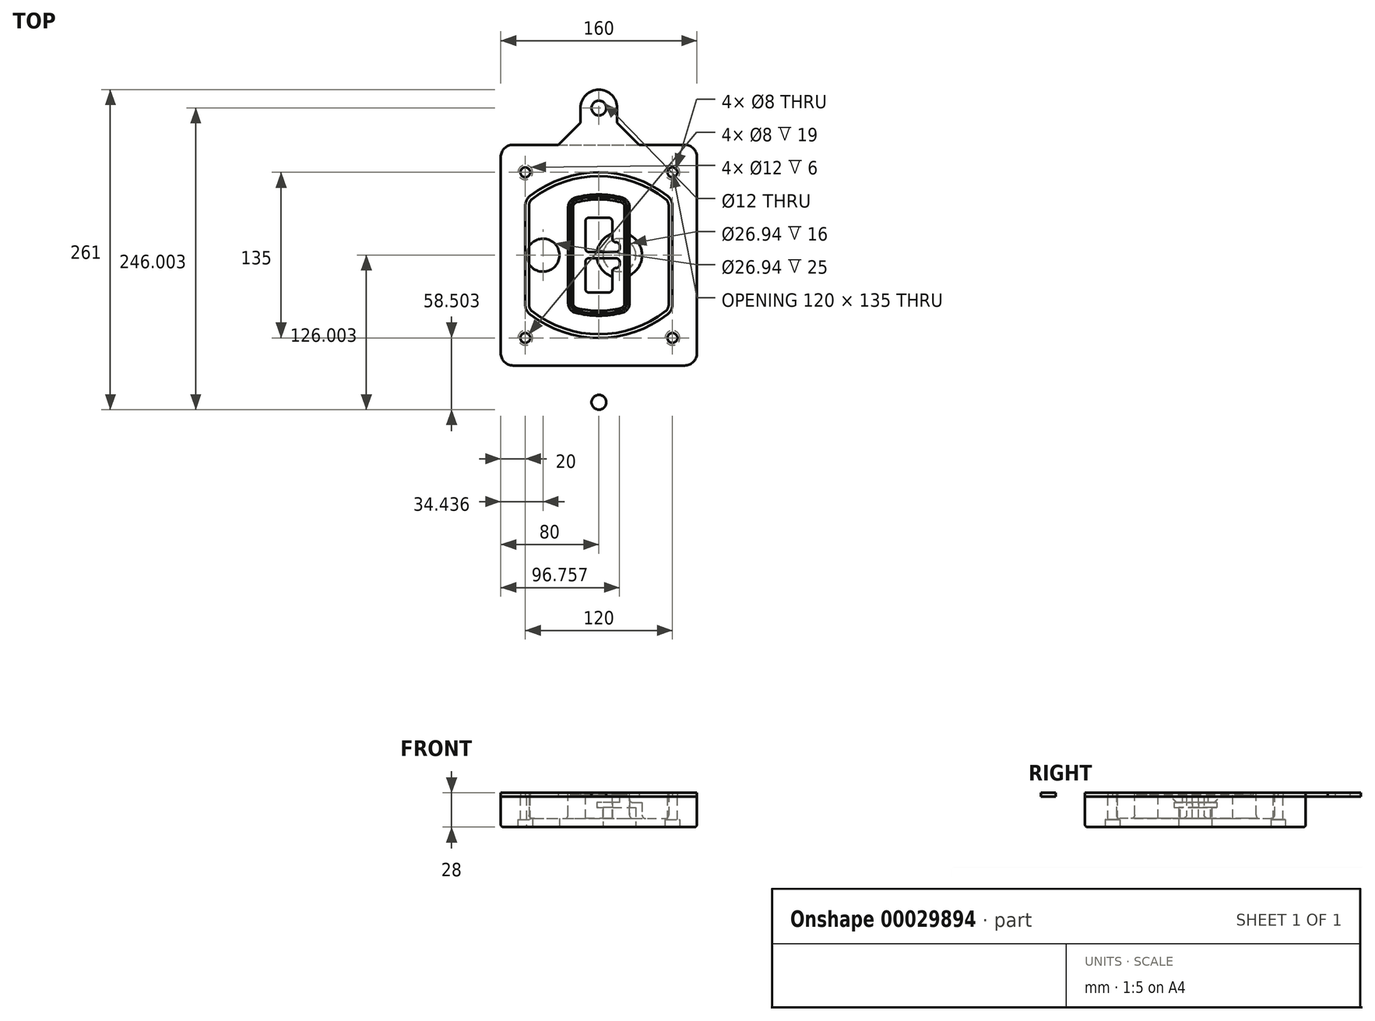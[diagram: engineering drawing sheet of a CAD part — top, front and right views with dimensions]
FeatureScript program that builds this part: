
annotation { "Feature Type Name" : "Feature", "Feature Type Description" : "" }
export const myFeature = defineFeature(function(context is Context, id is Id, definition is map)
    precondition{}
    {
        {
            var Q0;
            Q0=qCreatedBy(makeId("Top.planeOp"),FACE);
            var sketch = newSketch(context, id + "F0", { "sketchPlane" : qUnion([Q0])});
            skPoint(sketch, "E0.rect.middle", {"position": v(0, 0) * mm});
            skLineSegment(sketch, "E1.bottom", {"start": v(24.05, 28.38) * mm, "end": v(164.05, 28.38) * mm});
            skLineSegment(sketch, "E1.top", {"start": v(24.05, 208.38) * mm, "end": v(164.05, 208.38) * mm});
            skLineSegment(sketch, "E1.left", {"start": v(14.05, 38.38) * mm, "end": v(14.05, 198.38) * mm});
            skLineSegment(sketch, "E1.right", {"start": v(174.05, 38.38) * mm, "end": v(174.05, 198.38) * mm});
            skLineSegment(sketch, "E2", {"start": v(14.05, 208.38) * mm, "end": v(174.05, 28.38) * mm, "construction": true});
            skLineSegment(sketch, "E3", {"start": v(174.05, 208.38) * mm, "end": v(14.05, 28.38) * mm, "construction": true});
            skCircle(sketch, "E4", {"center": v(34.05, 185.88) * mm, "radius": 4 * mm});
            skCircle(sketch, "E5", {"center": v(154.05, 185.88) * mm, "radius": 4 * mm});
            skCircle(sketch, "E6", {"center": v(154.05, 50.88) * mm, "radius": 4 * mm});
            skCircle(sketch, "E7", {"center": v(34.05, 50.88) * mm, "radius": 4 * mm});
            skLineSegment(sketch, "E8", {"start": v(34.05, 185.88) * mm, "end": v(154.05, 185.88) * mm, "construction": true});
            skLineSegment(sketch, "E9", {"start": v(154.05, 185.88) * mm, "end": v(154.05, 50.88) * mm, "construction": true});
            skLineSegment(sketch, "E10", {"start": v(154.05, 50.88) * mm, "end": v(34.05, 50.88) * mm, "construction": true});
            skLineSegment(sketch, "E11", {"start": v(34.05, 50.88) * mm, "end": v(34.05, 185.88) * mm, "construction": true});
            skLineSegment(sketch, "E12", {"start": v(34.05, 158.68) * mm, "end": v(34.05, 78.09) * mm});
            skLineSegment(sketch, "E13", {"start": v(154.05, 158.68) * mm, "end": v(154.05, 78.09) * mm});
            skArc(sketch, "E14", {"start": v(150.2, 166.56) * mm, "mid": v(94.05, 185.88) * mm, "end": v(37.9, 166.56) * mm});
            skArc(sketch, "E15", {"start": v(37.9, 70.2) * mm, "mid": v(94.05, 50.88) * mm, "end": v(150.2, 70.2) * mm});
            skLineSegment(sketch, "E16", {"start": v(34.05, 118.38) * mm, "end": v(154.05, 118.38) * mm, "construction": true});
            skPoint(sketch, "E17.visualSharp", {"position": v(34.05, 73.38) * mm});
            skArc(sketch, "E17.filletArc", {"start": v(34.05, 78.09) * mm, "mid": v(35.06, 73.7) * mm, "end": v(37.9, 70.2) * mm});
            skPoint(sketch, "E18.visualSharp", {"position": v(34.05, 163.38) * mm});
            skArc(sketch, "E18.filletArc", {"start": v(37.9, 166.56) * mm, "mid": v(35.06, 163.06) * mm, "end": v(34.05, 158.68) * mm});
            skPoint(sketch, "E19.visualSharp", {"position": v(154.05, 163.38) * mm});
            skArc(sketch, "E19.filletArc", {"start": v(154.05, 158.68) * mm, "mid": v(153.04, 163.06) * mm, "end": v(150.2, 166.56) * mm});
            skPoint(sketch, "E20.visualSharp", {"position": v(154.05, 73.38) * mm});
            skArc(sketch, "E20.filletArc", {"start": v(150.2, 70.2) * mm, "mid": v(153.04, 73.7) * mm, "end": v(154.05, 78.09) * mm});
            skPoint(sketch, "E21.visualSharp", {"position": v(14.05, 208.38) * mm});
            skArc(sketch, "E21.filletArc", {"start": v(24.05, 208.38) * mm, "mid": v(16.98, 205.45) * mm, "end": v(14.05, 198.38) * mm});
            skPoint(sketch, "E22.visualSharp", {"position": v(174.05, 208.38) * mm});
            skArc(sketch, "E22.filletArc", {"start": v(174.05, 198.38) * mm, "mid": v(171.12, 205.45) * mm, "end": v(164.05, 208.38) * mm});
            skPoint(sketch, "E23.visualSharp", {"position": v(174.05, 28.38) * mm});
            skArc(sketch, "E23.filletArc", {"start": v(164.05, 28.38) * mm, "mid": v(171.12, 31.31) * mm, "end": v(174.05, 38.38) * mm});
            skPoint(sketch, "E24.visualSharp", {"position": v(14.05, 28.38) * mm});
            skArc(sketch, "E24.filletArc", {"start": v(14.05, 38.38) * mm, "mid": v(16.98, 31.31) * mm, "end": v(24.05, 28.38) * mm});
            skArc(sketch, "E25.0", {"start": v(151.05, 158.68) * mm, "mid": v(150.34, 161.75) * mm, "end": v(148.36, 164.2) * mm});
            skLineSegment(sketch, "E25.1", {"start": v(151.05, 158.68) * mm, "end": v(151.05, 78.09) * mm});
            skArc(sketch, "E25.2", {"start": v(148.36, 72.57) * mm, "mid": v(150.34, 75.02) * mm, "end": v(151.05, 78.09) * mm});
            skArc(sketch, "E25.3", {"start": v(39.74, 72.57) * mm, "mid": v(94.05, 53.88) * mm, "end": v(148.36, 72.57) * mm});
            skArc(sketch, "E25.4", {"start": v(37.05, 78.09) * mm, "mid": v(37.76, 75.02) * mm, "end": v(39.74, 72.57) * mm});
            skArc(sketch, "E25.5", {"start": v(148.36, 164.2) * mm, "mid": v(94.05, 182.88) * mm, "end": v(39.74, 164.2) * mm});
            skLineSegment(sketch, "E25.6", {"start": v(37.05, 158.68) * mm, "end": v(37.05, 78.09) * mm});
            skArc(sketch, "E25.7", {"start": v(39.74, 164.2) * mm, "mid": v(37.76, 161.75) * mm, "end": v(37.05, 158.68) * mm});
            skArc(sketch, "E26.0", {"start": v(35.43, 169.71) * mm, "mid": v(31.47, 164.82) * mm, "end": v(30.05, 158.68) * mm});
            skArc(sketch, "E26.1", {"start": v(152.67, 169.71) * mm, "mid": v(94.05, 189.88) * mm, "end": v(35.43, 169.71) * mm});
            skArc(sketch, "E26.2", {"start": v(158.05, 158.68) * mm, "mid": v(156.63, 164.82) * mm, "end": v(152.67, 169.71) * mm});
            skLineSegment(sketch, "E26.3", {"start": v(158.05, 158.68) * mm, "end": v(158.05, 78.09) * mm});
            skArc(sketch, "E26.4", {"start": v(152.67, 67.05) * mm, "mid": v(156.63, 71.95) * mm, "end": v(158.05, 78.09) * mm});
            skLineSegment(sketch, "E26.5", {"start": v(30.05, 158.68) * mm, "end": v(30.05, 78.09) * mm});
            skArc(sketch, "E26.6", {"start": v(35.43, 67.05) * mm, "mid": v(94.05, 46.88) * mm, "end": v(152.67, 67.05) * mm});
            skArc(sketch, "E26.7", {"start": v(30.05, 78.09) * mm, "mid": v(31.47, 71.95) * mm, "end": v(35.43, 67.05) * mm});
            skSolve(sketch);
        }
        {
            var Q0;
            Q0=makeQuery(id+"F0.imprint","IMPRINT",FACE,{"disambiguationData":[TD([[makeQuery(id+"F0.imprint","IMPRINT",EDGE,{"derivedFrom":sQuery(id+"F0.wireOp",EDGE,"E1.bottom")}),1.0]])]});
            var Q1;
            Q1=makeQuery(id+"F0.imprint","IMPRINT",FACE,{"disambiguationData":[TD([[makeQuery(id+"F0.imprint","IMPRINT",EDGE,{"derivedFrom":sQuery(id+"F0.wireOp",EDGE,"E12")}),1.0]])]});
            var Q2;
            Q2=makeQuery(id+"F0.imprint","IMPRINT",FACE,{"disambiguationData":[TD([[makeQuery(id+"F0.imprint","IMPRINT",EDGE,{"derivedFrom":sQuery(id+"F0.wireOp",EDGE,"E25.0")}),1.0]])]});
            var Q3;
            Q3=makeQuery(id+"F0.imprint","IMPRINT",FACE,{"disambiguationData":[TD([[makeQuery(id+"F0.imprint","IMPRINT",EDGE,{"derivedFrom":sQuery(id+"F0.wireOp",EDGE,"E12")}),-1.0]])]});
            extrude(context, id + "F1", {"entities" : qUnion([Q0, Q1, Q2, Q3]), "oppositeDirection" : true, "depth" : 25 * mm});
        }
        {
            var Q0;
            Q0=makeQuery(id+"F0.imprint","IMPRINT",FACE,{"disambiguationData":[TD([[makeQuery(id+"F0.imprint","IMPRINT",EDGE,{"derivedFrom":sQuery(id+"F0.wireOp",EDGE,"E12")}),1.0]])]});
            extrude(context, id + "F2", {"entities" : qUnion([Q0]), "operationType" : NewBodyOperationType.ADD, "depth" : 3 * mm});
        }
        {
            var Q0;
            Q0=makeQuery(id+"F0.imprint","IMPRINT",FACE,{"disambiguationData":[TD([[makeQuery(id+"F0.imprint","IMPRINT",EDGE,{"derivedFrom":sQuery(id+"F0.wireOp",EDGE,"E25.0")}),1.0]])]});
            extrude(context, id + "F3", {"entities" : qUnion([Q0]), "operationType" : NewBodyOperationType.REMOVE, "oppositeDirection" : true, "depth" : 18 * mm});
        }
        {
            var Q0;
            Q0=makeQuery(id+"F2.opExtrude","CAP_FACE",FACE,{"disambiguationData":[OSD([sQuery(id+"F0.wireOp",EDGE,"E12"),sQuery(id+"F0.wireOp",EDGE,"E13"),sQuery(id+"F0.wireOp",EDGE,"E14"),sQuery(id+"F0.wireOp",EDGE,"E15"),sQuery(id+"F0.wireOp",EDGE,"E17.filletArc"),sQuery(id+"F0.wireOp",EDGE,"E18.filletArc"),sQuery(id+"F0.wireOp",EDGE,"E19.filletArc"),sQuery(id+"F0.wireOp",EDGE,"E20.filletArc"),sQuery(id+"F0.wireOp",EDGE,"E25.0"),sQuery(id+"F0.wireOp",EDGE,"E25.1"),sQuery(id+"F0.wireOp",EDGE,"E25.2"),sQuery(id+"F0.wireOp",EDGE,"E25.3"),sQuery(id+"F0.wireOp",EDGE,"E25.4"),sQuery(id+"F0.wireOp",EDGE,"E25.5"),sQuery(id+"F0.wireOp",EDGE,"E25.6"),sQuery(id+"F0.wireOp",EDGE,"E25.7")])],"isStart":false});
            var sketch = newSketch(context, id + "F4", { "sketchPlane" : qUnion([Q0])});
            skArc(sketch, "E27.0", {"start": v(74.97, 71.41) * mm, "mid": v(94.05, 68.88) * mm, "end": v(113.13, 71.41) * mm});
            skArc(sketch, "E28.0", {"start": v(113.13, 165.35) * mm, "mid": v(94.05, 167.88) * mm, "end": v(74.97, 165.35) * mm});
            skLineSegment(sketch, "E29", {"start": v(69.05, 157.63) * mm, "end": v(69.05, 79.14) * mm});
            skLineSegment(sketch, "E30", {"start": v(119.05, 157.63) * mm, "end": v(119.05, 79.14) * mm});
            skLineSegment(sketch, "E31", {"start": v(69.05, 163.48) * mm, "end": v(119.05, 163.48) * mm, "construction": true});
            skLineSegment(sketch, "E32", {"start": v(69.05, 73.28) * mm, "end": v(119.05, 73.28) * mm, "construction": true});
            skPoint(sketch, "E33.visualSharp", {"position": v(69.05, 163.48) * mm});
            skArc(sketch, "E33.filletArc", {"start": v(74.97, 165.35) * mm, "mid": v(70.7, 162.5) * mm, "end": v(69.05, 157.63) * mm});
            skPoint(sketch, "E34.visualSharp", {"position": v(119.05, 163.48) * mm});
            skArc(sketch, "E34.filletArc", {"start": v(119.05, 157.63) * mm, "mid": v(117.4, 162.5) * mm, "end": v(113.13, 165.35) * mm});
            skPoint(sketch, "E35.visualSharp", {"position": v(119.05, 73.28) * mm});
            skArc(sketch, "E35.filletArc", {"start": v(113.13, 71.41) * mm, "mid": v(117.4, 74.27) * mm, "end": v(119.05, 79.14) * mm});
            skPoint(sketch, "E36.visualSharp", {"position": v(69.05, 73.28) * mm});
            skArc(sketch, "E36.filletArc", {"start": v(69.05, 79.14) * mm, "mid": v(70.7, 74.27) * mm, "end": v(74.97, 71.41) * mm});
            skArc(sketch, "E37.0", {"start": v(148.36, 164.2) * mm, "mid": v(94.05, 182.88) * mm, "end": v(39.74, 164.2) * mm});
            skArc(sketch, "E37.1", {"start": v(39.74, 164.2) * mm, "mid": v(37.76, 161.75) * mm, "end": v(37.05, 158.68) * mm});
            skLineSegment(sketch, "E37.2", {"start": v(37.05, 158.68) * mm, "end": v(37.05, 78.09) * mm});
            skArc(sketch, "E37.3", {"start": v(37.05, 78.09) * mm, "mid": v(37.76, 75.02) * mm, "end": v(39.74, 72.57) * mm});
            skArc(sketch, "E37.4", {"start": v(39.74, 72.57) * mm, "mid": v(94.05, 53.88) * mm, "end": v(148.36, 72.57) * mm});
            skArc(sketch, "E37.5", {"start": v(148.36, 72.57) * mm, "mid": v(150.34, 75.02) * mm, "end": v(151.05, 78.09) * mm});
            skLineSegment(sketch, "E37.6", {"start": v(151.05, 158.68) * mm, "end": v(151.05, 78.09) * mm});
            skArc(sketch, "E37.7", {"start": v(151.05, 158.68) * mm, "mid": v(150.34, 161.75) * mm, "end": v(148.36, 164.2) * mm});
            skLineSegment(sketch, "E38.0", {"start": v(117.05, 157.63) * mm, "end": v(117.05, 79.14) * mm});
            skArc(sketch, "E38.1", {"start": v(112.61, 73.34) * mm, "mid": v(115.81, 75.49) * mm, "end": v(117.05, 79.14) * mm});
            skArc(sketch, "E38.2", {"start": v(75.49, 73.34) * mm, "mid": v(94.05, 70.88) * mm, "end": v(112.61, 73.34) * mm});
            skArc(sketch, "E38.3", {"start": v(71.05, 79.14) * mm, "mid": v(72.29, 75.49) * mm, "end": v(75.49, 73.34) * mm});
            skLineSegment(sketch, "E38.4", {"start": v(71.05, 157.63) * mm, "end": v(71.05, 79.14) * mm});
            skArc(sketch, "E38.5", {"start": v(117.05, 157.63) * mm, "mid": v(115.81, 161.28) * mm, "end": v(112.61, 163.42) * mm});
            skArc(sketch, "E38.6", {"start": v(75.49, 163.42) * mm, "mid": v(72.29, 161.28) * mm, "end": v(71.05, 157.63) * mm});
            skArc(sketch, "E38.7", {"start": v(112.61, 163.42) * mm, "mid": v(94.05, 165.88) * mm, "end": v(75.49, 163.42) * mm});
            skArc(sketch, "E39.0", {"start": v(115.05, 157.63) * mm, "mid": v(114.23, 160.06) * mm, "end": v(112.1, 161.5) * mm});
            skLineSegment(sketch, "E39.1", {"start": v(115.05, 157.63) * mm, "end": v(115.05, 79.14) * mm});
            skArc(sketch, "E39.2", {"start": v(112.1, 75.27) * mm, "mid": v(114.23, 76.7) * mm, "end": v(115.05, 79.14) * mm});
            skArc(sketch, "E39.3", {"start": v(76, 75.27) * mm, "mid": v(94.05, 72.88) * mm, "end": v(112.1, 75.27) * mm});
            skArc(sketch, "E39.4", {"start": v(73.05, 79.14) * mm, "mid": v(73.87, 76.7) * mm, "end": v(76, 75.27) * mm});
            skArc(sketch, "E39.5", {"start": v(112.1, 161.5) * mm, "mid": v(94.05, 163.88) * mm, "end": v(76, 161.5) * mm});
            skLineSegment(sketch, "E39.6", {"start": v(73.05, 157.63) * mm, "end": v(73.05, 79.14) * mm});
            skArc(sketch, "E39.7", {"start": v(76, 161.5) * mm, "mid": v(73.87, 160.06) * mm, "end": v(73.05, 157.63) * mm});
            skLineSegment(sketch, "E40", {"start": v(69.05, 118.38) * mm, "end": v(119.05, 118.38) * mm, "construction": true});
            skLineSegment(sketch, "E41", {"start": v(83.05, 123.88) * mm, "end": v(83.05, 145.88) * mm});
            skLineSegment(sketch, "E42", {"start": v(86.05, 148.88) * mm, "end": v(102.05, 148.88) * mm});
            skLineSegment(sketch, "E43", {"start": v(105.05, 145.88) * mm, "end": v(105.05, 131.88) * mm});
            skLineSegment(sketch, "E44", {"start": v(108.05, 128.88) * mm, "end": v(108.05, 128.88) * mm});
            skLineSegment(sketch, "E45", {"start": v(111.05, 125.88) * mm, "end": v(111.05, 123.88) * mm});
            skLineSegment(sketch, "E46", {"start": v(108.05, 120.88) * mm, "end": v(86.05, 120.88) * mm});
            skPoint(sketch, "E47.visualSharp", {"position": v(83.05, 148.88) * mm});
            skArc(sketch, "E47.filletArc", {"start": v(86.05, 148.88) * mm, "mid": v(83.93, 148) * mm, "end": v(83.05, 145.88) * mm});
            skPoint(sketch, "E48.visualSharp", {"position": v(105.05, 148.88) * mm});
            skArc(sketch, "E48.filletArc", {"start": v(105.05, 145.88) * mm, "mid": v(104.17, 148) * mm, "end": v(102.05, 148.88) * mm});
            skPoint(sketch, "E49.visualSharp", {"position": v(105.05, 128.88) * mm});
            skArc(sketch, "E49.filletArc", {"start": v(105.05, 131.88) * mm, "mid": v(105.93, 129.76) * mm, "end": v(108.05, 128.88) * mm});
            skPoint(sketch, "E50.visualSharp", {"position": v(111.05, 128.88) * mm});
            skArc(sketch, "E50.filletArc", {"start": v(111.05, 125.88) * mm, "mid": v(110.17, 128) * mm, "end": v(108.05, 128.88) * mm});
            skPoint(sketch, "E51.visualSharp", {"position": v(111.05, 120.88) * mm});
            skArc(sketch, "E51.filletArc", {"start": v(108.05, 120.88) * mm, "mid": v(110.17, 121.76) * mm, "end": v(111.05, 123.88) * mm});
            skPoint(sketch, "E52.visualSharp", {"position": v(83.05, 120.88) * mm});
            skArc(sketch, "E52.filletArc", {"start": v(83.05, 123.88) * mm, "mid": v(83.93, 121.76) * mm, "end": v(86.05, 120.88) * mm});
            skLineSegment(sketch, "E53.0.MirrorCS", {"start": v(108.05, 115.88) * mm, "end": v(86.05, 115.88) * mm});
            skArc(sketch, "E54.0.MirrorCS", {"start": v(83.05, 112.88) * mm, "mid": v(83.93, 115) * mm, "end": v(86.05, 115.88) * mm});
            skLineSegment(sketch, "E55.0.MirrorCS", {"start": v(83.05, 112.88) * mm, "end": v(83.05, 90.88) * mm});
            skArc(sketch, "E56.0.MirrorCS", {"start": v(86.05, 87.88) * mm, "mid": v(83.93, 88.76) * mm, "end": v(83.05, 90.88) * mm});
            skLineSegment(sketch, "E57.0.MirrorCS", {"start": v(86.05, 87.88) * mm, "end": v(102.05, 87.88) * mm});
            skArc(sketch, "E58.0.MirrorCS", {"start": v(105.05, 90.88) * mm, "mid": v(104.17, 88.76) * mm, "end": v(102.05, 87.88) * mm});
            skLineSegment(sketch, "E59.0.MirrorCS", {"start": v(105.05, 90.88) * mm, "end": v(105.05, 104.88) * mm});
            skArc(sketch, "E60.0.MirrorCS", {"start": v(105.05, 104.88) * mm, "mid": v(105.93, 107) * mm, "end": v(108.05, 107.88) * mm});
            skArc(sketch, "E61.0.MirrorCS", {"start": v(111.05, 110.88) * mm, "mid": v(110.17, 108.76) * mm, "end": v(108.05, 107.88) * mm});
            skLineSegment(sketch, "E62.0.MirrorCS", {"start": v(111.05, 110.88) * mm, "end": v(111.05, 112.88) * mm});
            skArc(sketch, "E63.0.MirrorCS", {"start": v(108.05, 115.88) * mm, "mid": v(110.17, 115) * mm, "end": v(111.05, 112.88) * mm});
            skSolve(sketch);
        }
        {
            var Q0;
            Q0=makeQuery(id+"F4.imprint","IMPRINT",FACE,{"disambiguationData":[TD([[makeQuery(id+"F4.imprint","IMPRINT",EDGE,{"derivedFrom":sQuery(id+"F4.wireOp",EDGE,"E27.0")}),1.0]])]});
            var Q1;
            Q1=makeQuery(id+"F4.imprint","IMPRINT",FACE,{"disambiguationData":[TD([[makeQuery(id+"F4.imprint","IMPRINT",EDGE,{"derivedFrom":sQuery(id+"F4.wireOp",EDGE,"E38.0")}),-1.0]])]});
            var Q2;
            Q2=makeQuery(id+"F4.imprint","IMPRINT",FACE,{"disambiguationData":[TD([[makeQuery(id+"F4.imprint","IMPRINT",EDGE,{"derivedFrom":sQuery(id+"F4.wireOp",EDGE,"E39.0")}),1.0]])]});
            extrude(context, id + "F5", {"entities" : qUnion([Q0, Q1, Q2]), "operationType" : NewBodyOperationType.ADD, "endBound" : BoundingType.UP_TO_NEXT, "oppositeDirection" : true, "depth" : 25 * mm});
        }
        {
            var Q0;
            Q0=makeQuery(id+"F4.imprint","IMPRINT",FACE,{"disambiguationData":[TD([[makeQuery(id+"F4.imprint","IMPRINT",EDGE,{"derivedFrom":sQuery(id+"F4.wireOp",EDGE,"E38.0")}),-1.0]])]});
            extrude(context, id + "F6", {"entities" : qUnion([Q0]), "operationType" : NewBodyOperationType.REMOVE, "oppositeDirection" : true, "depth" : 2 * mm});
        }
        {
            var Q0;
            Q0=makeQuery(id+"F1.opExtrude","CAP_FACE",FACE,{"disambiguationData":[OSD([sQuery(id+"F0.wireOp",EDGE,"E1.bottom"),sQuery(id+"F0.wireOp",EDGE,"E1.top"),sQuery(id+"F0.wireOp",EDGE,"E1.left"),sQuery(id+"F0.wireOp",EDGE,"E1.right"),sQuery(id+"F0.wireOp",EDGE,"E4"),sQuery(id+"F0.wireOp",EDGE,"E5"),sQuery(id+"F0.wireOp",EDGE,"E6"),sQuery(id+"F0.wireOp",EDGE,"E7"),sQuery(id+"F0.wireOp",EDGE,"E21.filletArc"),sQuery(id+"F0.wireOp",EDGE,"E22.filletArc"),sQuery(id+"F0.wireOp",EDGE,"E23.filletArc"),sQuery(id+"F0.wireOp",EDGE,"E24.filletArc")])],"isStart":false});
            var sketch = newSketch(context, id + "F7", { "sketchPlane" : qUnion([Q0])});
            skCircle(sketch, "E64", {"center": v(110.8, -118.38) * mm, "radius": 13.47 * mm});
            skCircle(sketch, "E65", {"center": v(48.49, -118.38) * mm, "radius": 13.47 * mm});
            skLineSegment(sketch, "E66", {"start": v(174.05, -118.38) * mm, "end": v(14.05, -118.38) * mm});
            skCircle(sketch, "E67", {"center": v(110.8, -118.38) * mm, "radius": 18.47 * mm});
            skCircle(sketch, "E68", {"center": v(154.05, -185.88) * mm, "radius": 6 * mm});
            skCircle(sketch, "E69", {"center": v(34.05, -185.88) * mm, "radius": 6 * mm});
            skCircle(sketch, "E70", {"center": v(34.05, -50.88) * mm, "radius": 6 * mm});
            skCircle(sketch, "E71", {"center": v(154.05, -50.88) * mm, "radius": 6 * mm});
            skSolve(sketch);
        }
        {
            var Q0;
            {var subQ1=sQuery(id+"F7.wireOp",EDGE,"E66");var subQ4=sQuery(id+"F7.wireOp",EDGE,"E64");var subQ6=makeQuery(id+"F7.imprint","INTERSECT",VERTEX,{"disambiguationData":[OD(0.0)],"derivedFrom":[subQ4,subQ1]});Q0=makeQuery(id+"F7.imprint","IMPRINT",FACE,{"disambiguationData":[TD([[makeQuery(id+"F7.imprint","IMPRINT",EDGE,{"disambiguationData":[TD([[subQ6,-1.0]])],"derivedFrom":subQ4}),-1.0]])]});}
            var Q1;
            {var subQ0=sQuery(id+"F7.wireOp",EDGE,"E66");var subQ1=sQuery(id+"F7.wireOp",EDGE,"E64");var subQ3=makeQuery(id+"F7.imprint","INTERSECT",VERTEX,{"disambiguationData":[OD(0.0)],"derivedFrom":[subQ1,subQ0]});Q1=makeQuery(id+"F7.imprint","IMPRINT",FACE,{"disambiguationData":[TD([[makeQuery(id+"F7.imprint","IMPRINT",EDGE,{"disambiguationData":[TD([[subQ3,-1.0]])],"derivedFrom":subQ1}),1.0]])]});}
            var Q2;
            {var subQ0=sQuery(id+"F7.wireOp",EDGE,"E66");var subQ1=sQuery(id+"F7.wireOp",EDGE,"E64");var subQ3=makeQuery(id+"F7.imprint","INTERSECT",VERTEX,{"disambiguationData":[OD(0.0)],"derivedFrom":[subQ1,subQ0]});Q2=makeQuery(id+"F7.imprint","IMPRINT",FACE,{"disambiguationData":[TD([[makeQuery(id+"F7.imprint","IMPRINT",EDGE,{"disambiguationData":[TD([[subQ3,1.0]])],"derivedFrom":subQ1}),1.0]])]});}
            var Q3;
            {var subQ1=sQuery(id+"F7.wireOp",EDGE,"E66");var subQ4=sQuery(id+"F7.wireOp",EDGE,"E64");var subQ6=makeQuery(id+"F7.imprint","INTERSECT",VERTEX,{"disambiguationData":[OD(0.0)],"derivedFrom":[subQ4,subQ1]});Q3=makeQuery(id+"F7.imprint","IMPRINT",FACE,{"disambiguationData":[TD([[makeQuery(id+"F7.imprint","IMPRINT",EDGE,{"disambiguationData":[TD([[subQ6,1.0]])],"derivedFrom":subQ4}),-1.0]])]});}
            extrude(context, id + "F8", {"entities" : qUnion([Q0, Q1, Q2, Q3]), "operationType" : NewBodyOperationType.ADD, "oppositeDirection" : true, "depth" : 20 * mm});
        }
        {
            var Q0;
            {var subQ0=sQuery(id+"F7.wireOp",EDGE,"E66");var subQ1=sQuery(id+"F7.wireOp",EDGE,"E64");var subQ3=makeQuery(id+"F7.imprint","INTERSECT",VERTEX,{"disambiguationData":[OD(0.0)],"derivedFrom":[subQ1,subQ0]});Q0=makeQuery(id+"F7.imprint","IMPRINT",FACE,{"disambiguationData":[TD([[makeQuery(id+"F7.imprint","IMPRINT",EDGE,{"disambiguationData":[TD([[subQ3,-1.0]])],"derivedFrom":subQ1}),1.0]])]});}
            var Q1;
            {var subQ0=sQuery(id+"F7.wireOp",EDGE,"E66");var subQ1=sQuery(id+"F7.wireOp",EDGE,"E64");var subQ3=makeQuery(id+"F7.imprint","INTERSECT",VERTEX,{"disambiguationData":[OD(0.0)],"derivedFrom":[subQ1,subQ0]});Q1=makeQuery(id+"F7.imprint","IMPRINT",FACE,{"disambiguationData":[TD([[makeQuery(id+"F7.imprint","IMPRINT",EDGE,{"disambiguationData":[TD([[subQ3,1.0]])],"derivedFrom":subQ1}),1.0]])]});}
            extrude(context, id + "F9", {"entities" : qUnion([Q0, Q1]), "operationType" : NewBodyOperationType.REMOVE, "oppositeDirection" : true, "depth" : 16 * mm});
        }
        {
            var Q0;
            {var subQ0=sQuery(id+"F7.wireOp",EDGE,"E66");var subQ1=sQuery(id+"F7.wireOp",EDGE,"E65");var subQ3=makeQuery(id+"F7.imprint","INTERSECT",VERTEX,{"disambiguationData":[OD(0.0)],"derivedFrom":[subQ1,subQ0]});Q0=makeQuery(id+"F7.imprint","IMPRINT",FACE,{"disambiguationData":[TD([[makeQuery(id+"F7.imprint","IMPRINT",EDGE,{"disambiguationData":[TD([[subQ3,-1.0]])],"derivedFrom":subQ1}),1.0]])]});}
            var Q1;
            {var subQ0=sQuery(id+"F7.wireOp",EDGE,"E66");var subQ1=sQuery(id+"F7.wireOp",EDGE,"E65");var subQ3=makeQuery(id+"F7.imprint","INTERSECT",VERTEX,{"disambiguationData":[OD(0.0)],"derivedFrom":[subQ1,subQ0]});Q1=makeQuery(id+"F7.imprint","IMPRINT",FACE,{"disambiguationData":[TD([[makeQuery(id+"F7.imprint","IMPRINT",EDGE,{"disambiguationData":[TD([[subQ3,1.0]])],"derivedFrom":subQ1}),1.0]])]});}
            extrude(context, id + "F10", {"entities" : qUnion([Q0, Q1]), "operationType" : NewBodyOperationType.REMOVE, "oppositeDirection" : true, "depth" : 25 * mm});
        }
        {
            var Q0;
            Q0=makeQuery(id+"F7.imprint","IMPRINT",FACE,{"disambiguationData":[TD([[makeQuery(id+"F7.imprint","IMPRINT",EDGE,{"derivedFrom":sQuery(id+"F7.wireOp",EDGE,"E68")}),1.0]])]});
            var Q1;
            Q1=makeQuery(id+"F7.imprint","IMPRINT",FACE,{"disambiguationData":[TD([[makeQuery(id+"F7.imprint","IMPRINT",EDGE,{"derivedFrom":makeQuery(id+"F1.opExtrude","CAP_EDGE",EDGE,{"disambiguationData":[OSD([sQuery(id+"F0.wireOp",EDGE,"E5")])],"isStart":false})}),-1.0]])]});
            var Q2;
            Q2=makeQuery(id+"F7.imprint","IMPRINT",FACE,{"disambiguationData":[TD([[makeQuery(id+"F7.imprint","IMPRINT",EDGE,{"derivedFrom":sQuery(id+"F7.wireOp",EDGE,"E69")}),1.0]])]});
            var Q3;
            Q3=makeQuery(id+"F7.imprint","IMPRINT",FACE,{"disambiguationData":[TD([[makeQuery(id+"F7.imprint","IMPRINT",EDGE,{"derivedFrom":makeQuery(id+"F1.opExtrude","CAP_EDGE",EDGE,{"disambiguationData":[OSD([sQuery(id+"F0.wireOp",EDGE,"E4")])],"isStart":false})}),-1.0]])]});
            var Q4;
            Q4=makeQuery(id+"F7.imprint","IMPRINT",FACE,{"disambiguationData":[TD([[makeQuery(id+"F7.imprint","IMPRINT",EDGE,{"derivedFrom":sQuery(id+"F7.wireOp",EDGE,"E70")}),1.0]])]});
            var Q5;
            Q5=makeQuery(id+"F7.imprint","IMPRINT",FACE,{"disambiguationData":[TD([[makeQuery(id+"F7.imprint","IMPRINT",EDGE,{"derivedFrom":makeQuery(id+"F1.opExtrude","CAP_EDGE",EDGE,{"disambiguationData":[OSD([sQuery(id+"F0.wireOp",EDGE,"E7")])],"isStart":false})}),-1.0]])]});
            var Q6;
            Q6=makeQuery(id+"F7.imprint","IMPRINT",FACE,{"disambiguationData":[TD([[makeQuery(id+"F7.imprint","IMPRINT",EDGE,{"derivedFrom":sQuery(id+"F7.wireOp",EDGE,"E71")}),1.0]])]});
            var Q7;
            Q7=makeQuery(id+"F7.imprint","IMPRINT",FACE,{"disambiguationData":[TD([[makeQuery(id+"F7.imprint","IMPRINT",EDGE,{"derivedFrom":makeQuery(id+"F1.opExtrude","CAP_EDGE",EDGE,{"disambiguationData":[OSD([sQuery(id+"F0.wireOp",EDGE,"E6")])],"isStart":false})}),-1.0]])]});
            extrude(context, id + "F11", {"entities" : qUnion([Q0, Q1, Q2, Q3, Q4, Q5, Q6, Q7]), "operationType" : NewBodyOperationType.REMOVE, "oppositeDirection" : true, "depth" : 6 * mm});
        }
        {
            var Q0;
            Q0=makeQuery(id+"F9.boolean.opBoolean","COPY",FACE,{"derivedFrom":makeQuery(id+"F9.opExtrude","CAP_FACE",FACE,{"disambiguationData":[OSD([sQuery(id+"F7.wireOp",EDGE,"E64")])],"isStart":false})});
            var sketch = newSketch(context, id + "F12", { "sketchPlane" : qUnion([Q0])});
            skArc(sketch, "E72.0", {"start": v(105.05, -100.83) * mm, "mid": v(96.62, -106.56) * mm, "end": v(92.5, -115.88) * mm});
            skArc(sketch, "E72.1", {"start": v(92.5, -120.88) * mm, "mid": v(96.62, -130.2) * mm, "end": v(105.05, -135.93) * mm});
            skLineSegment(sketch, "E73", {"start": v(92.5, -120.88) * mm, "end": v(108.05, -120.88) * mm});
            skLineSegment(sketch, "E74.0", {"start": v(108.05, -115.88) * mm, "end": v(92.5, -115.88) * mm});
            skArc(sketch, "E74.1", {"start": v(108.05, -115.88) * mm, "mid": v(110.17, -115) * mm, "end": v(111.05, -112.88) * mm});
            skLineSegment(sketch, "E74.2", {"start": v(111.05, -110.88) * mm, "end": v(111.05, -112.88) * mm});
            skArc(sketch, "E74.3", {"start": v(111.05, -110.88) * mm, "mid": v(110.17, -108.76) * mm, "end": v(108.05, -107.88) * mm});
            skArc(sketch, "E74.4", {"start": v(105.05, -104.88) * mm, "mid": v(105.93, -107) * mm, "end": v(108.05, -107.88) * mm});
            skLineSegment(sketch, "E74.5", {"start": v(105.05, -100.83) * mm, "end": v(105.05, -104.88) * mm});
            skLineSegment(sketch, "E74.7", {"start": v(108.05, -120.88) * mm, "end": v(92.5, -120.88) * mm});
            skArc(sketch, "E74.8", {"start": v(108.05, -120.88) * mm, "mid": v(110.17, -121.76) * mm, "end": v(111.05, -123.88) * mm});
            skLineSegment(sketch, "E74.9", {"start": v(111.05, -125.88) * mm, "end": v(111.05, -123.88) * mm});
            skArc(sketch, "E74.10", {"start": v(111.05, -125.88) * mm, "mid": v(110.17, -128) * mm, "end": v(108.05, -128.88) * mm});
            skArc(sketch, "E74.11", {"start": v(105.05, -131.88) * mm, "mid": v(105.93, -129.76) * mm, "end": v(108.05, -128.88) * mm});
            skLineSegment(sketch, "E74.12", {"start": v(105.05, -135.93) * mm, "end": v(105.05, -131.88) * mm});
            skPoint(sketch, "E75.orphan", {"position": v(105.05, -145.88) * mm});
            skPoint(sketch, "E76.orphan", {"position": v(86.05, -120.88) * mm});
            skPoint(sketch, "E77.orphan", {"position": v(86.05, -115.88) * mm});
            skPoint(sketch, "E78.orphan", {"position": v(105.05, -90.88) * mm});
            skSolve(sketch);
        }
        {
            var Q0;
            {var subQ7=sQuery(id+"F12.wireOp",EDGE,"E72.0");var subQ14=sQuery(id+"F12.wireOp",EDGE,"E72.1");var subQ16=sQuery(id+"F12.wireOp",EDGE,"E74.1");var subQ18=sQuery(id+"F12.wireOp",EDGE,"E74.8");Q0=qUnion([makeQuery(id+"F12.imprint","IMPRINT",FACE,{"disambiguationData":[TD([[makeQuery(id+"F12.imprint","IMPRINT",EDGE,{"derivedFrom":subQ7}),1.0]])]}),makeQuery(id+"F12.imprint","IMPRINT",FACE,{"disambiguationData":[TD([[makeQuery(id+"F12.imprint","IMPRINT",EDGE,{"derivedFrom":subQ14}),1.0]])]}),makeQuery(id+"F12.imprint","IMPRINT",FACE,{"disambiguationData":[TD([[makeQuery(id+"F12.imprint","IMPRINT",EDGE,{"derivedFrom":subQ16}),1.0]])]}),makeQuery(id+"F12.imprint","IMPRINT",FACE,{"disambiguationData":[TD([[makeQuery(id+"F12.imprint","IMPRINT",EDGE,{"derivedFrom":subQ18}),-1.0]])]})]);}
            var Q1;
            Q1=makeQuery(id+"F5.boolean.opBoolean","SPLIT",FACE,{"disambiguationData":[TD([makeQuery(id+"F5.opExtrude","SWEPT_FACE",FACE,{"disambiguationData":[OSD([sQuery(id+"F4.wireOp",EDGE,"E41")])]})])],"derivedFrom":makeQuery(id+"F3.boolean.opBoolean","COPY",FACE,{"derivedFrom":makeQuery(id+"F3.opExtrude","CAP_FACE",FACE,{"disambiguationData":[OSD([sQuery(id+"F0.wireOp",EDGE,"E25.0"),sQuery(id+"F0.wireOp",EDGE,"E25.1"),sQuery(id+"F0.wireOp",EDGE,"E25.2"),sQuery(id+"F0.wireOp",EDGE,"E25.3"),sQuery(id+"F0.wireOp",EDGE,"E25.4"),sQuery(id+"F0.wireOp",EDGE,"E25.5"),sQuery(id+"F0.wireOp",EDGE,"E25.6"),sQuery(id+"F0.wireOp",EDGE,"E25.7")])],"isStart":false})})});
            extrude(context, id + "F13", {"entities" : qUnion([Q0]), "operationType" : NewBodyOperationType.REMOVE, "endBound" : BoundingType.UP_TO_SURFACE, "endBoundEntityFace" : qUnion([Q1]), "depth" : 25 * mm});
        }
        {
            var Q0;
            Q0=makeQuery(id+"F3.boolean.opBoolean","COPY",EDGE,{"derivedFrom":makeQuery(id+"F3.opExtrude","CAP_EDGE",EDGE,{"disambiguationData":[OSD([sQuery(id+"F0.wireOp",EDGE,"E25.6")])],"isStart":false})});
            var Q1;
            Q1=makeQuery(id+"F8.boolean.opBoolean","INTERSECT",EDGE,{"derivedFrom":[makeQuery(id+"F5.opExtrude","SWEPT_FACE",FACE,{"disambiguationData":[OSD([sQuery(id+"F4.wireOp",EDGE,"E30")])]}),makeQuery(id+"F8.opExtrude","CAP_FACE",FACE,{"disambiguationData":[OSD([sQuery(id+"F7.wireOp",EDGE,"E67")])],"isStart":false})]});
            var Q2;
            Q2=makeQuery(id+"F8.boolean.opBoolean","INTERSECT",EDGE,{"disambiguationData":[OD(1.0)],"derivedFrom":[makeQuery(id+"F5.opExtrude","SWEPT_FACE",FACE,{"disambiguationData":[OSD([sQuery(id+"F4.wireOp",EDGE,"E30")])]}),makeQuery(id+"F8.opExtrude","SWEPT_FACE",FACE,{"disambiguationData":[OSD([sQuery(id+"F7.wireOp",EDGE,"E67")])]})]});
            var Q3;
            {var subQ0=sQuery(id+"F4.wireOp",EDGE,"E30");Q3=makeQuery(id+"F8.boolean.opBoolean","SPLIT",EDGE,{"disambiguationData":[TD([makeQuery(id+"F5.opExtrude","SWEPT_FACE",FACE,{"disambiguationData":[OSD([sQuery(id+"F4.wireOp",EDGE,"E35.filletArc")])]})])],"derivedFrom":makeQuery(id+"F5.opExtrude","CAP_EDGE",EDGE,{"disambiguationData":[OSD([subQ0])],"isStart":false})});}
            var Q4;
            {var subQ0=sQuery(id+"F0.wireOp",EDGE,"E25.7");var subQ1=sQuery(id+"F0.wireOp",EDGE,"E25.1");var subQ2=sQuery(id+"F0.wireOp",EDGE,"E25.6");var subQ3=sQuery(id+"F0.wireOp",EDGE,"E25.5");var subQ4=sQuery(id+"F0.wireOp",EDGE,"E25.4");var subQ5=sQuery(id+"F0.wireOp",EDGE,"E25.0");var subQ6=sQuery(id+"F0.wireOp",EDGE,"E25.2");var subQ7=sQuery(id+"F0.wireOp",EDGE,"E25.3");Q4=makeQuery(id+"F8.boolean.opBoolean","INTERSECT",EDGE,{"derivedFrom":[makeQuery(id+"F5.boolean.opBoolean","SPLIT",FACE,{"disambiguationData":[TD([makeQuery(id+"F2.opExtrude","SWEPT_FACE",FACE,{"disambiguationData":[OSD([subQ5])]})])],"derivedFrom":makeQuery(id+"F3.boolean.opBoolean","COPY",FACE,{"derivedFrom":makeQuery(id+"F3.opExtrude","CAP_FACE",FACE,{"disambiguationData":[OSD([subQ5,subQ1,subQ6,subQ7,subQ4,subQ3,subQ2,subQ0])],"isStart":false})})}),makeQuery(id+"F8.opExtrude","SWEPT_FACE",FACE,{"disambiguationData":[OSD([sQuery(id+"F7.wireOp",EDGE,"E67")])]})]});}
            var Q5;
            Q5=makeQuery(id+"F8.boolean.opBoolean","INTERSECT",EDGE,{"disambiguationData":[OD(0.0)],"derivedFrom":[makeQuery(id+"F5.opExtrude","SWEPT_FACE",FACE,{"disambiguationData":[OSD([sQuery(id+"F4.wireOp",EDGE,"E30")])]}),makeQuery(id+"F8.opExtrude","SWEPT_FACE",FACE,{"disambiguationData":[OSD([sQuery(id+"F7.wireOp",EDGE,"E67")])]})]});
            fillet(context, id + "F14", {"entities" : qUnion([Q0, Q1, Q2, Q3, Q4, Q5]), "radius" : 3 * mm, "tangentPropagation" : true, "allowEdgeOverflow" : false});
        }
        {
            var Q0;
            Q0=makeQuery(id+"F1.opExtrude","CAP_EDGE",EDGE,{"disambiguationData":[OSD([sQuery(id+"F0.wireOp",EDGE,"E1.bottom")])],"isStart":false});
            fillet(context, id + "F15", {"entities" : qUnion([Q0]), "radius" : 2 * mm, "tangentPropagation" : true, "allowEdgeOverflow" : false});
        }
        {
            var Q0;
            {var subQ0=sQuery(id+"F0.wireOp",EDGE,"E1.bottom");var subQ1=sQuery(id+"F0.wireOp",EDGE,"E1.top");var subQ2=sQuery(id+"F0.wireOp",EDGE,"E1.left");var subQ3=sQuery(id+"F0.wireOp",EDGE,"E1.right");var subQ4=sQuery(id+"F0.wireOp",EDGE,"E4");var subQ5=sQuery(id+"F0.wireOp",EDGE,"E5");var subQ6=sQuery(id+"F0.wireOp",EDGE,"E6");var subQ7=sQuery(id+"F0.wireOp",EDGE,"E7");var subQ8=sQuery(id+"F0.wireOp",EDGE,"E21.filletArc");var subQ9=sQuery(id+"F0.wireOp",EDGE,"E22.filletArc");var subQ10=sQuery(id+"F0.wireOp",EDGE,"E23.filletArc");var subQ11=sQuery(id+"F0.wireOp",EDGE,"E24.filletArc");Q0=makeQuery(id+"F2.boolean.opBoolean","SPLIT",FACE,{"disambiguationData":[TD([makeQuery(id+"F1.opExtrude","SWEPT_FACE",FACE,{"disambiguationData":[OSD([subQ0])]})])],"derivedFrom":makeQuery(id+"F1.opExtrude","CAP_FACE",FACE,{"disambiguationData":[OSD([subQ0,subQ1,subQ2,subQ3,subQ4,subQ5,subQ6,subQ7,subQ8,subQ9,subQ10,subQ11])],"isStart":true})});}
            var sketch = newSketch(context, id + "F16", { "sketchPlane" : qUnion([Q0])});
            skLineSegment(sketch, "E79", {"start": v(94.05, 208.38) * mm, "end": v(94.05, 238.38) * mm, "construction": true});
            skCircle(sketch, "E80", {"center": v(94.05, 238.38) * mm, "radius": 6 * mm});
            skLineSegment(sketch, "E81", {"start": v(109.05, 238.38) * mm, "end": v(109.05, 226.38) * mm});
            skLineSegment(sketch, "E82", {"start": v(109.05, 226.38) * mm, "end": v(127.05, 208.38) * mm});
            skLineSegment(sketch, "E83", {"start": v(79.05, 238.38) * mm, "end": v(79.05, 226.38) * mm});
            skArc(sketch, "E84", {"start": v(109.05, 238.38) * mm, "mid": v(94.05, 253.38) * mm, "end": v(79.05, 238.38) * mm});
            skLineSegment(sketch, "E85.MirrorCS", {"start": v(79.05, 226.38) * mm, "end": v(61.05, 208.38) * mm});
            skLineSegment(sketch, "E86", {"start": v(14.05, 118.38) * mm, "end": v(174.05, 118.38) * mm, "construction": true});
            skLineSegment(sketch, "E87.MirrorCS", {"start": v(94.05, 28.38) * mm, "end": v(94.05, -1.62) * mm, "construction": true});
            skCircle(sketch, "E88.MirrorC", {"center": v(94.05, -1.62) * mm, "radius": 6 * mm});
            skLineSegment(sketch, "E89.MirrorCS", {"start": v(79.05, 10.38) * mm, "end": v(61.05, 28.38) * mm});
            skArc(sketch, "E90.MirrorCS", {"start": v(109.05, -1.62) * mm, "mid": v(94.05, -16.62) * mm, "end": v(79.05, -1.62) * mm});
            skLineSegment(sketch, "E91.MirrorCS", {"start": v(79.05, -1.62) * mm, "end": v(79.05, 10.38) * mm});
            skLineSegment(sketch, "E92.MirrorCS", {"start": v(109.05, -1.62) * mm, "end": v(109.05, 10.38) * mm});
            skLineSegment(sketch, "E93.MirrorCS", {"start": v(109.05, 10.38) * mm, "end": v(127.05, 28.38) * mm});
            skSolve(sketch);
        }
        {
            var Q0;
            Q0=makeQuery(id+"F16.imprint","IMPRINT",FACE,{"disambiguationData":[TD([[makeQuery(id+"F16.imprint","IMPRINT",EDGE,{"derivedFrom":sQuery(id+"F16.wireOp",EDGE,"E88.MirrorC")}),1.0]])]});
            var Q1;
            Q1=makeQuery(id+"F16.imprint","IMPRINT",FACE,{"disambiguationData":[TD([[makeQuery(id+"F16.imprint","IMPRINT",EDGE,{"derivedFrom":sQuery(id+"F16.wireOp",EDGE,"E80")}),-1.0]])]});
            var Q2;
            Q2=makeQuery(id+"F16.imprint","IMPRINT",FACE,{"disambiguationData":[TD([[makeQuery(id+"F16.imprint","IMPRINT",EDGE,{"derivedFrom":makeQuery(id+"F1.opExtrude","CAP_EDGE",EDGE,{"disambiguationData":[OSD([sQuery(id+"F0.wireOp",EDGE,"E1.left")])],"isStart":true})}),-1.0]])]});
            var Q3;
            Q3=makeQuery(id+"F2.opExtrude","CAP_FACE",FACE,{"disambiguationData":[OSD([sQuery(id+"F0.wireOp",EDGE,"E12"),sQuery(id+"F0.wireOp",EDGE,"E13"),sQuery(id+"F0.wireOp",EDGE,"E14"),sQuery(id+"F0.wireOp",EDGE,"E15"),sQuery(id+"F0.wireOp",EDGE,"E17.filletArc"),sQuery(id+"F0.wireOp",EDGE,"E18.filletArc"),sQuery(id+"F0.wireOp",EDGE,"E19.filletArc"),sQuery(id+"F0.wireOp",EDGE,"E20.filletArc"),sQuery(id+"F0.wireOp",EDGE,"E25.0"),sQuery(id+"F0.wireOp",EDGE,"E25.1"),sQuery(id+"F0.wireOp",EDGE,"E25.2"),sQuery(id+"F0.wireOp",EDGE,"E25.3"),sQuery(id+"F0.wireOp",EDGE,"E25.4"),sQuery(id+"F0.wireOp",EDGE,"E25.5"),sQuery(id+"F0.wireOp",EDGE,"E25.6"),sQuery(id+"F0.wireOp",EDGE,"E25.7")])],"isStart":false});
            extrude(context, id + "F17", {"entities" : qUnion([Q0, Q1, Q2]), "endBound" : BoundingType.UP_TO_SURFACE, "endBoundEntityFace" : qUnion([Q3]), "depth" : 25 * mm});
        }
    });
